# Revit family: Dauphin_TecIdentity_TaskChair_CleanRoom
name_source: partatom
category: Furniture
units: mm (PartAtom-declared; Revit-internal decimal feet)

## family parameters
Always vertical = Yes
Cut with Voids When Loaded = No
Enable Cutting in Views = No
OmniClass Number = 23.40.20.00
OmniClass Title = General Furniture and Specialties
Render Appearance Source = Family Geometry
Room Calculation Point = No
Shared = No
Work Plane-Based = No

## types (1)
- Dauphin-IS 2023_CNR Tec  identity, work chair, backrest with plastic on outside, non-conductive Cleanroom.
    Arm pads material = dgxkusto543ec444
    Arms = No
    Article = IS 2023_CNR SE NV T6 SR  KGS A114KGS FPAPO S64CR R70WGS 313033 313033 V12 ZIDHO
    Casters material = dgxpvcgrd77d2ef8
    Default Elevation = 0 mm  [stored 0 ft]
    Description = CNR Work chair
    Gas lift cover material = dgxacr76568f5a
    Gas spring material = dgxapo5f5522af
    J Bar Height Guide = dgxzidho268482d7
    Manufacturer = Dauphin
    Model = IS 2023_CNR
    OFML-FamilyCreationDate = 20260209
    OFML-FamilyCreationVersion = 8.13/2.1.0
    Revision = 1.0.0
    Seat support material = dgxpvcblee902366
    Seat upholstery = dgx3130328bb569f

note: [stored X ft] marks values corroborated as IEEE doubles in the binary element streams (Revit-internal decimal feet)

## geometry (parser evidence)
native form markers: Sweep x2
no freeform markers — native parametric forms only
